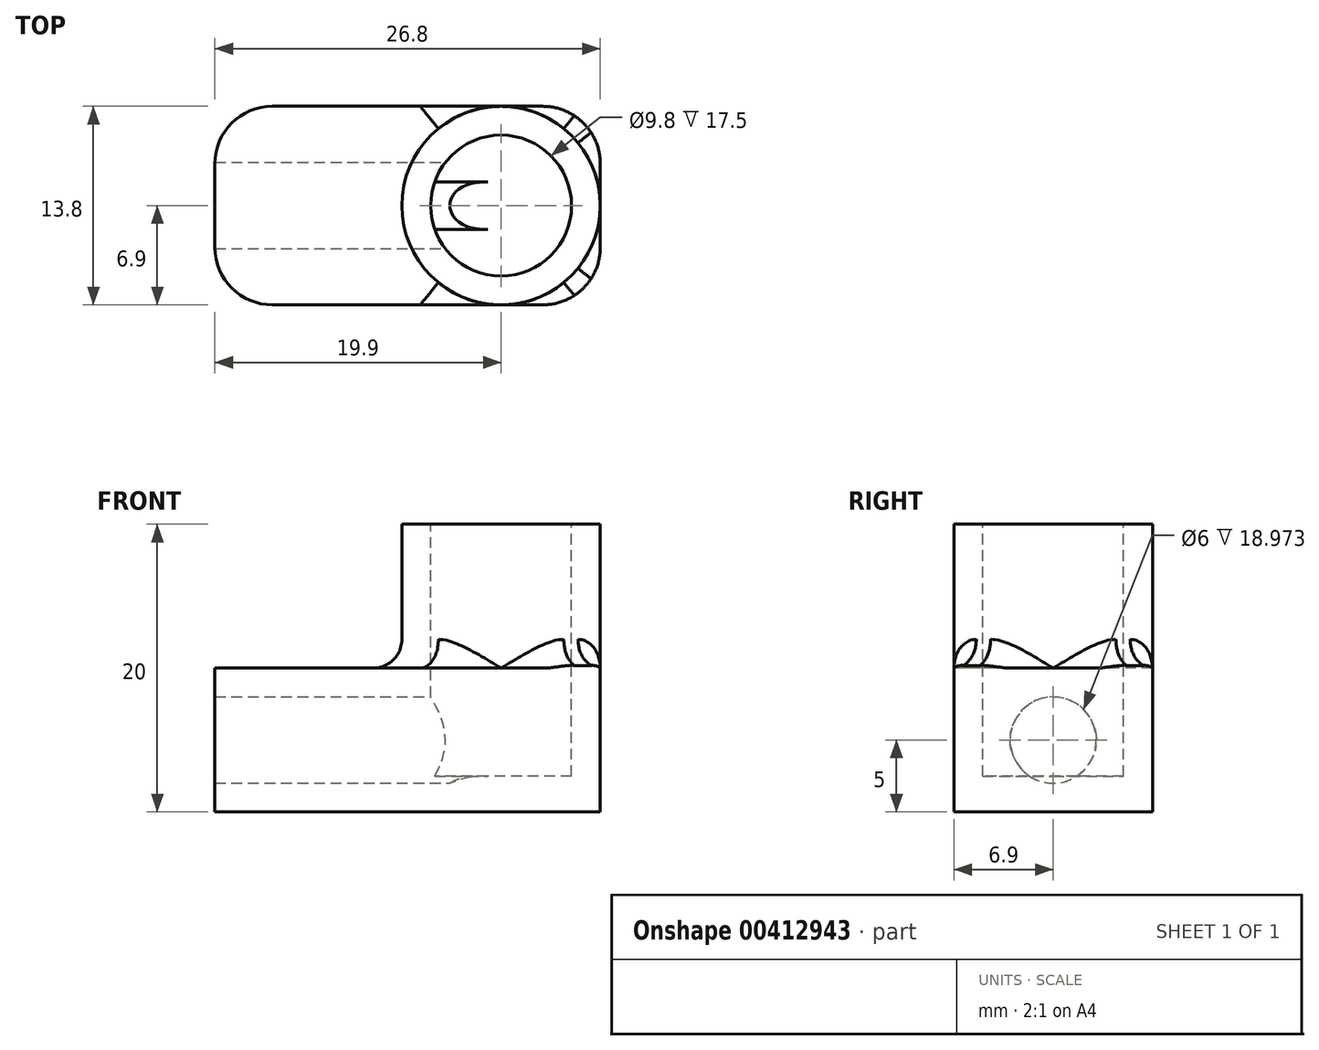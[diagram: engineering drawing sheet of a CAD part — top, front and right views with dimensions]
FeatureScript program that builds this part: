
annotation { "Feature Type Name" : "Feature", "Feature Type Description" : "" }
export const myFeature = defineFeature(function(context is Context, id is Id, definition is map)
    precondition{}
    {
        {
            var Q0;
            Q0=qCreatedBy(makeId("Top.planeOp"),FACE);
            var sketch = newSketch(context, id + "F0", { "sketchPlane" : qUnion([Q0])});
            skCircle(sketch, "E0", {"center": v(0, 0) * mm, "radius": 4.9 * mm});
            skCircle(sketch, "E1", {"center": v(0, 0) * mm, "radius": 6.9 * mm});
            skLineSegment(sketch, "E2.bottom", {"start": v(6.9, -6.9) * mm, "end": v(-6.9, -6.9) * mm});
            skLineSegment(sketch, "E2.top", {"start": v(6.9, 6.9) * mm, "end": v(-6.9, 6.9) * mm});
            skLineSegment(sketch, "E2.left", {"start": v(6.9, -6.9) * mm, "end": v(6.9, 6.9) * mm});
            skLineSegment(sketch, "E2.right", {"start": v(-6.9, -6.9) * mm, "end": v(-6.9, 6.9) * mm});
            skSolve(sketch);
        }
        {
            var Q0;
            Q0 = qSketchRegion(id + "F0", true);
            var Q1;
            Q1=makeQuery(id+"F0.imprint","IMPRINT",FACE,{"disambiguationData":[TD([[makeQuery(id+"F0.imprint","IMPRINT",EDGE,{"derivedFrom":sQuery(id+"F0.wireOp",EDGE,"E0")}),-1.0]])]});
            extrude(context, id + "F1", {"entities" : qUnion([Q0, Q1]), "oppositeDirection" : true, "depth" : 10 * mm, "offsetDistance" : 25 * mm});
        }
        {
            var Q0;
            Q0=makeQuery(id+"F0.imprint","IMPRINT",FACE,{"disambiguationData":[TD([[makeQuery(id+"F0.imprint","IMPRINT",EDGE,{"derivedFrom":sQuery(id+"F0.wireOp",EDGE,"E0")}),-1.0]])]});
            extrude(context, id + "F2", {"entities" : qUnion([Q0]), "operationType" : NewBodyOperationType.ADD, "depth" : 10 * mm, "offsetDistance" : 25 * mm});
        }
        {
            var Q0;
            Q0=makeQuery(id+"F1.opExtrude","SWEPT_FACE",FACE,{"disambiguationData":[OSD([sQuery(id+"F0.wireOp",EDGE,"E2.right")])]});
            var sketch = newSketch(context, id + "F3", { "sketchPlane" : qUnion([Q0])});
            skPoint(sketch, "E3", {"position": v(-6.9, -5) * mm});
            skCircle(sketch, "E4", {"center": v(0, -5) * mm, "radius": 3 * mm});
            skPoint(sketch, "E5", {"position": v(0, 0) * mm});
            skSolve(sketch);
        }
        {
            var Q0;
            Q0=makeQuery(id+"F3.imprint","IMPRINT",FACE,{"disambiguationData":[TD([[makeQuery(id+"F3.imprint","IMPRINT",EDGE,{"derivedFrom":sQuery(id+"F3.wireOp",EDGE,"E4")}),-1.0]])]});
            extrude(context, id + "F4", {"entities" : qUnion([Q0]), "operationType" : NewBodyOperationType.ADD, "depth" : 13 * mm, "offsetDistance" : 25 * mm});
        }
        {
            var Q0;
            Q0=makeQuery(id+"F1.opExtrude","SWEPT_FACE",FACE,{"disambiguationData":[OSD([sQuery(id+"F0.wireOp",EDGE,"E2.right")])]});
            extrude(context, id + "F5", {"entities" : qUnion([Q0]), "operationType" : NewBodyOperationType.REMOVE, "endBound" : BoundingType.UP_TO_NEXT, "oppositeDirection" : true, "depth" : 25 * mm, "offsetDistance" : 25 * mm});
        }
        {
            var Q0;
            Q0=makeQuery(id+"F0.imprint","IMPRINT",FACE,{"disambiguationData":[TD([[makeQuery(id+"F0.imprint","IMPRINT",EDGE,{"derivedFrom":sQuery(id+"F0.wireOp",EDGE,"E0")}),1.0]])]});
            var Q1;
            {var subQ0=sQuery(id+"F0.wireOp",EDGE,"E2.right");Q1=makeQuery(id+"F4.boolean.opBoolean","MERGE",FACE,{"derivedFrom":[makeQuery(id+"F1.opExtrude","CAP_FACE",FACE,{"disambiguationData":[OSD([sQuery(id+"F0.wireOp",EDGE,"E0"),sQuery(id+"F0.wireOp",EDGE,"E2.bottom"),sQuery(id+"F0.wireOp",EDGE,"E2.top"),sQuery(id+"F0.wireOp",EDGE,"E2.left"),subQ0])],"isStart":false}),makeQuery(id+"F4.opExtrude","SWEPT_FACE",FACE,{"disambiguationData":[OSD([subQ0])]})]});}
            var Q2;
            {var subQ0=sQuery(id+"F3.wireOp",EDGE,"E4");Q2=makeQuery(id+"F5.boolean.opBoolean","MERGE",FACE,{"derivedFrom":[makeQuery(id+"F4.opExtrude","SWEPT_FACE",FACE,{"disambiguationData":[OSD([subQ0])]})],"fromTools":[makeQuery(id+"F5.opExtrude","SWEPT_FACE",FACE,{"disambiguationData":[OSD([subQ0])]})]});}
            extrude(context, id + "F6", {"entities" : qUnion([Q0]), "operationType" : NewBodyOperationType.ADD, "endBound" : BoundingType.UP_TO_SURFACE, "oppositeDirection" : true, "depth" : 25 * mm, "endBoundEntityFace" : qUnion([Q1]), "offsetDistance" : 25 * mm, "hasSecondDirection" : true, "secondDirectionOppositeDirection" : true, "secondDirectionDepth" : 7.5 * mm, "secondDirectionBoundEntityFace" : qUnion([Q2])});
        }
        {
            var Q0;
            {var subQ0=sQuery(id+"F0.wireOp",EDGE,"E2.left");var subQ1=sQuery(id+"F0.wireOp",EDGE,"E2.top");var subQ2=sQuery(id+"F0.wireOp",EDGE,"E1");Q0=makeQuery(id+"F2.boolean.opBoolean","SPLIT",EDGE,{"disambiguationData":[TD([makeQuery(id+"F1.opExtrude","CAP_FACE",FACE,{"disambiguationData":[OSD([sQuery(id+"F0.wireOp",EDGE,"E0"),sQuery(id+"F0.wireOp",EDGE,"E2.bottom"),subQ1,subQ0,sQuery(id+"F0.wireOp",EDGE,"E2.right")])],"isStart":true}),makeQuery(id+"F1.opExtrude","SWEPT_FACE",FACE,{"disambiguationData":[OSD([subQ1])]}),makeQuery(id+"F1.opExtrude","SWEPT_FACE",FACE,{"disambiguationData":[OSD([subQ0])]}),makeQuery(id+"F2.opExtrude","SWEPT_FACE",FACE,{"disambiguationData":[OSD([subQ2])]})])],"derivedFrom":makeQuery(id+"F2.opExtrude","CAP_EDGE",EDGE,{"disambiguationData":[OSD([subQ2])],"isStart":true})});}
            fillet(context, id + "F7", {"entities" : qUnion([Q0]), "tangentPropagation" : true, "radius" : 2 * mm, "defaultsChanged" : true, "vertexSettings" : [], "allowEdgeOverflow" : false});
        }
        {
            var Q0;
            {var subQ0=sQuery(id+"F0.wireOp",EDGE,"E0");Q0=makeQuery(id+"F6.boolean.opBoolean","SPLIT",EDGE,{"disambiguationData":[topologyDisambiguationEdgeConnected([makeQuery(id+"F1.opExtrude","SWEPT_FACE",FACE,{"disambiguationData":[OSD([subQ0])]})])],"derivedFrom":makeQuery(id+"F6.opExtrude","CAP_EDGE",EDGE,{"disambiguationData":[OSD([subQ0])],"isStart":true})});}
            fillet(context, id + "F8", {"entities" : qUnion([Q0]), "tangentPropagation" : true, "radius" : 3 * mm, "defaultsChanged" : true, "vertexSettings" : [], "allowEdgeOverflow" : false});
        }
        {
            var Q0;
            Q0=makeQuery(id+"F1.opExtrude","SWEPT_EDGE",EDGE,{"disambiguationData":[OSD([sQuery(id+"F0.wireOp",EDGE,"E2.bottom"),sQuery(id+"F0.wireOp",EDGE,"E2.left")])]});
            var Q1;
            Q1=makeQuery(id+"F1.opExtrude","SWEPT_EDGE",EDGE,{"disambiguationData":[OSD([sQuery(id+"F0.wireOp",EDGE,"E2.top"),sQuery(id+"F0.wireOp",EDGE,"E2.left")])]});
            var Q2;
            Q2=makeQuery(id+"F4.opExtrude","CAP_EDGE",EDGE,{"disambiguationData":[OSD([sQuery(id+"F0.wireOp",EDGE,"E2.bottom"),sQuery(id+"F0.wireOp",EDGE,"E2.right")])],"isStart":false});
            var Q3;
            Q3=makeQuery(id+"F4.opExtrude","CAP_EDGE",EDGE,{"disambiguationData":[OSD([sQuery(id+"F0.wireOp",EDGE,"E2.top"),sQuery(id+"F0.wireOp",EDGE,"E2.right")])],"isStart":false});
            fillet(context, id + "F9", {"entities" : qUnion([Q0, Q1, Q2, Q3]), "tangentPropagation" : true, "radius" : 4 * mm, "defaultsChanged" : false, "vertexSettings" : [], "allowEdgeOverflow" : false});
        }
    });
